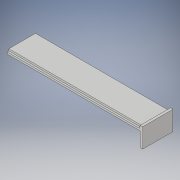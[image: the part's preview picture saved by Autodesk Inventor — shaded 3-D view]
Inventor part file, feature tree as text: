
AUTODESK INVENTOR PART (.ipt)
format: ipt  version: 2019 (Build 230136000, 136)  size: 272,384 bytes
history: native  units: mm
features: extrude x3, sketch x3, mirror x1
ambient origin geometry x8: Origin, YZ Plane, XZ Plane, XY Plane, X Axis, Y Axis, Z Axis, Center Point
bodies: Solid1 (feature_tree)
feature tree (7):
  extrude  "Extrusion1"  Depth=22.0mm
  extrude  "Extrusion2"  Depth=1.5mm
  mirror  "Mirror1"
  extrude  "Extrusion4"  Depth=2.75mm
  sketch  "Sketch2"  dims[d2=112.0mm d3=22.0mm]
  sketch  "Sketch4"  dims[d4=3.0mm d5=0.0mm d6=1.5mm]
  sketch  "Sketch6"  dims[d7=1.5mm d8=0.0mm d12=2.75mm d13=2.0mm d14=12.0mm d15=0.0mm d16=4.0mm d17=0.0mm]
